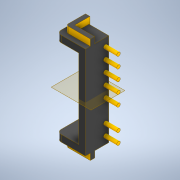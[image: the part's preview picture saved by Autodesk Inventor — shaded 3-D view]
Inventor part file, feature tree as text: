
AUTODESK INVENTOR PART (.ipt)
format: ipt  version: 2022 (Build 260153000, 153)  size: 237,568 bytes
history: native  units: mm
features: extrude x5, sketch x4, other x2
ambient origin geometry x8: Origin, YZ Plane, XZ Plane, XY Plane, X Axis, Y Axis, Z Axis, Center Point
bodies: Body1 (feature_tree)
feature tree (11):
  other  "Твердое тело1"
  extrude  "Выдавливание1"  Depth=1.0mm
  extrude  "Выдавливание2"  Depth=21.0mm TaperAngle=0.0deg
  extrude  "Выдавливание5"  Depth=1.425mm TaperAngle=0.0deg
  extrude  "Выдавливание6"  Depth=22.425mm TaperAngle=0.0deg
  other  "РабПлоскость1"
  extrude  "Выдавливание7"  Depth=5.0mm
  sketch  "Эскиз1"
  sketch  "Эскиз6"
  sketch  "Эскиз7"
  sketch  "Эскиз10"
